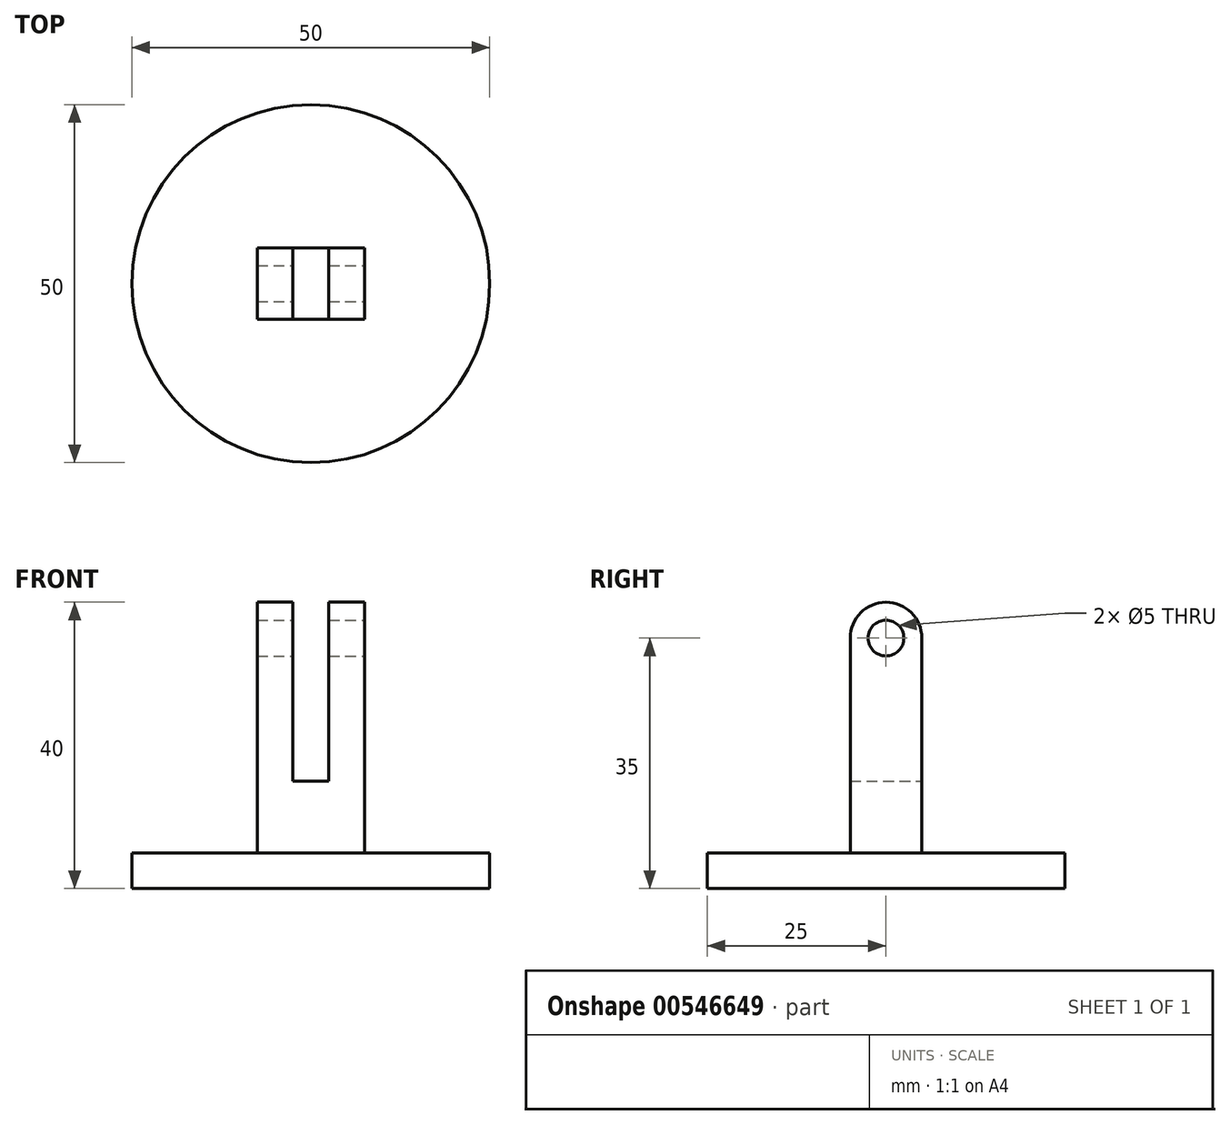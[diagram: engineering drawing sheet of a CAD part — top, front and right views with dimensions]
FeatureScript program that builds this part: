
annotation { "Feature Type Name" : "Feature", "Feature Type Description" : "" }
export const myFeature = defineFeature(function(context is Context, id is Id, definition is map)
    precondition{}
    {
        {
            var Q0;
            Q0=qCreatedBy(makeId("Top.planeOp"),FACE);
            var sketch = newSketch(context, id + "F0", { "sketchPlane" : qUnion([Q0])});
            skCircle(sketch, "E0", {"center": v(0, 0) * mm, "radius": 25 * mm});
            skSolve(sketch);
        }
        {
            var Q0;
            Q0=qCreatedBy(makeId("Top.planeOp"),FACE);
            var sketch = newSketch(context, id + "F1", { "sketchPlane" : qUnion([Q0])});
            skLineSegment(sketch, "E1.bottom", {"start": v(7.5, -5) * mm, "end": v(-7.5, -5) * mm});
            skLineSegment(sketch, "E1.top", {"start": v(7.5, 5) * mm, "end": v(-7.5, 5) * mm});
            skLineSegment(sketch, "E1.left", {"start": v(7.5, -5) * mm, "end": v(7.5, 5) * mm});
            skLineSegment(sketch, "E1.right", {"start": v(-7.5, -5) * mm, "end": v(-7.5, 5) * mm});
            skPoint(sketch, "E1.middle", {"position": v(0, 0) * mm});
            skSolve(sketch);
        }
        {
            var Q0;
            Q0=makeQuery(id+"F0.imprint","IMPRINT",FACE,{"disambiguationData":[TD([[makeQuery(id+"F0.imprint","IMPRINT",EDGE,{"derivedFrom":sQuery(id+"F0.wireOp",EDGE,"E0")}),1.0]])]});
            extrude(context, id + "F2", {"entities" : qUnion([Q0]), "depth" : 5 * mm, "offsetDistance" : 25 * mm});
        }
        {
            var Q0;
            Q0=makeQuery(id+"F1.imprint","IMPRINT",FACE,{"disambiguationData":[TD([[makeQuery(id+"F1.imprint","IMPRINT",EDGE,{"derivedFrom":sQuery(id+"F1.wireOp",EDGE,"E1.bottom")}),-1.0]])]});
            extrude(context, id + "F3", {"entities" : qUnion([Q0]), "operationType" : NewBodyOperationType.ADD, "depth" : 40 * mm, "offsetDistance" : 25 * mm});
        }
        {
            var Q0;
            Q0=makeQuery(id+"F3.opExtrude","CAP_FACE",FACE,{"disambiguationData":[OSD([sQuery(id+"F1.wireOp",EDGE,"E1.bottom"),sQuery(id+"F1.wireOp",EDGE,"E1.top"),sQuery(id+"F1.wireOp",EDGE,"E1.left"),sQuery(id+"F1.wireOp",EDGE,"E1.right")])],"isStart":false});
            var sketch = newSketch(context, id + "F4", { "sketchPlane" : qUnion([Q0])});
            skLineSegment(sketch, "E2.bottom", {"start": v(2.5, -5) * mm, "end": v(-2.5, -5) * mm});
            skLineSegment(sketch, "E2.top", {"start": v(2.5, 5) * mm, "end": v(-2.5, 5) * mm});
            skLineSegment(sketch, "E2.left", {"start": v(2.5, -5) * mm, "end": v(2.5, 5) * mm});
            skLineSegment(sketch, "E2.right", {"start": v(-2.5, -5) * mm, "end": v(-2.5, 5) * mm});
            skPoint(sketch, "E2.middle", {"position": v(0, 0) * mm});
            skSolve(sketch);
        }
        {
            var Q0;
            Q0=makeQuery(id+"F4.imprint","IMPRINT",FACE,{"disambiguationData":[TD([[makeQuery(id+"F4.imprint","IMPRINT",EDGE,{"derivedFrom":sQuery(id+"F4.wireOp",EDGE,"E2.bottom")}),-1.0]])]});
            extrude(context, id + "F5", {"entities" : qUnion([Q0]), "operationType" : NewBodyOperationType.REMOVE, "oppositeDirection" : true, "depth" : 25 * mm, "offsetDistance" : 25 * mm});
        }
        {
            var Q0;
            Q0=makeQuery(id+"F3.opExtrude","SWEPT_FACE",FACE,{"disambiguationData":[OSD([sQuery(id+"F1.wireOp",EDGE,"E1.left")])]});
            var sketch = newSketch(context, id + "F6", { "sketchPlane" : qUnion([Q0])});
            skCircle(sketch, "E3", {"center": v(0, 35) * mm, "radius": 2.5 * mm});
            skPoint(sketch, "E3.centerSnap0", {"position": v(0, 40) * mm});
            skSolve(sketch);
        }
        {
            var Q0;
            Q0=makeQuery(id+"F6.imprint","IMPRINT",FACE,{"disambiguationData":[TD([[makeQuery(id+"F6.imprint","IMPRINT",EDGE,{"derivedFrom":sQuery(id+"F6.wireOp",EDGE,"E3")}),1.0]])]});
            extrude(context, id + "F7", {"entities" : qUnion([Q0]), "operationType" : NewBodyOperationType.REMOVE, "endBound" : BoundingType.THROUGH_ALL, "oppositeDirection" : true, "depth" : 25 * mm, "offsetDistance" : 25 * mm});
        }
        {
            var Q0;
            {var subQ0=sQuery(id+"F1.wireOp",EDGE,"E1.right");var subQ1=sQuery(id+"F1.wireOp",EDGE,"E1.top");Q0=makeQuery(id+"F5.boolean.opBoolean","SPLIT",EDGE,{"disambiguationData":[TD([makeQuery(id+"F3.opExtrude","SWEPT_FACE",FACE,{"disambiguationData":[OSD([subQ0])]})])],"derivedFrom":makeQuery(id+"F3.opExtrude","CAP_EDGE",EDGE,{"disambiguationData":[OSD([subQ1])],"isStart":false})});}
            var Q1;
            {var subQ0=sQuery(id+"F1.wireOp",EDGE,"E1.bottom");var subQ1=sQuery(id+"F1.wireOp",EDGE,"E1.right");Q1=makeQuery(id+"F5.boolean.opBoolean","SPLIT",EDGE,{"disambiguationData":[TD([makeQuery(id+"F3.opExtrude","SWEPT_FACE",FACE,{"disambiguationData":[OSD([subQ1])]})])],"derivedFrom":makeQuery(id+"F3.opExtrude","CAP_EDGE",EDGE,{"disambiguationData":[OSD([subQ0])],"isStart":false})});}
            var Q2;
            {var subQ0=sQuery(id+"F1.wireOp",EDGE,"E1.left");var subQ1=sQuery(id+"F1.wireOp",EDGE,"E1.top");Q2=makeQuery(id+"F5.boolean.opBoolean","SPLIT",EDGE,{"disambiguationData":[TD([makeQuery(id+"F3.opExtrude","SWEPT_FACE",FACE,{"disambiguationData":[OSD([subQ0])]})])],"derivedFrom":makeQuery(id+"F3.opExtrude","CAP_EDGE",EDGE,{"disambiguationData":[OSD([subQ1])],"isStart":false})});}
            var Q3;
            {var subQ0=sQuery(id+"F1.wireOp",EDGE,"E1.bottom");var subQ1=sQuery(id+"F1.wireOp",EDGE,"E1.left");Q3=makeQuery(id+"F5.boolean.opBoolean","SPLIT",EDGE,{"disambiguationData":[TD([makeQuery(id+"F3.opExtrude","SWEPT_FACE",FACE,{"disambiguationData":[OSD([subQ1])]})])],"derivedFrom":makeQuery(id+"F3.opExtrude","CAP_EDGE",EDGE,{"disambiguationData":[OSD([subQ0])],"isStart":false})});}
            fillet(context, id + "F8", {"entities" : qUnion([Q0, Q1, Q2, Q3]), "radius" : 5 * mm, "tangentPropagation" : true, "allowEdgeOverflow" : false});
        }
    });
